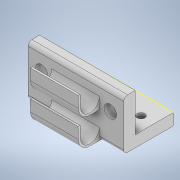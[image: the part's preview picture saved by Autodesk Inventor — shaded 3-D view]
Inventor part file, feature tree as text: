
AUTODESK INVENTOR PART (.ipt)
format: ipt  version: 2020 (Build 240168000, 168)  size: 246,784 bytes
history: native  units: in
note: dims shown in document units (in); Inventor stores cm internally (conversion verified against a paired STEP export)
features: sketch x7, extrude x4, plane x2, hole x2, direct_edit x1, fillet x1, mirror x1, move_body x1
ambient origin geometry x8: Origin, YZ Plane, XZ Plane, XY Plane, X Axis, Y Axis, Z Axis, Center Point
bodies: Solid1 (feature_tree)
feature tree (19):
  extrude  "Extrusion1"  Depth=1.0236in
  extrude  "Extrusion2"  Depth=0.7874in TaperAngle=0.0deg
  direct_edit  "Direct Edit1"
  extrude  "Extrusion7"  Depth=0.9843in
  plane  "Work Plane1"
  sketch  "Sketch8"  dims[d30=0.4724in d31=0.0in d45=0.3937in d58=0.0787in]
  extrude  "Extrusion15"  Depth=0.3937in
  fillet  "Fillet3"  Radius=0.0787in
  hole  "Hole1"  [1 undecoded]
  hole  "Hole2"  [1 undecoded]
  sketch  "Sketch13"  dims[d80=0.3937in d81=0.1969in d82=0.2362in d83=0.4724in d85=0.6322in d86=0.6322in d87=0.6322in d90=0.4724in d91=0.6322in d92=0.4724in d93=0.0in d94=0.0in d95=0.2362in d96=0.2362in d97=0.2756in d98=0.3937in d99=0.1575in d100=0.2362in d101=0.2559in d102=0.1772in d103=90.0deg d104=0.315in d105=0.8108in d106=0.2362in d107=0.3937in d108=0.2756in d109=0.1575in d110=0.2362in d111=0.2559in d112=0.1772in d113=90.0deg d114=0.315in d115=0.8108in d116=90.0deg d48=0.0197in d49=0.0344in d50=0.0197in d51=0.0344in d67=0.0197in d68=0.0344in d69=0.0197in d70=0.0344in d88=0.0197in d89=0.0344in]
  plane  "Work Plane3"
  mirror  "Mirror1"
  sketch  "Sketch1"  dims[d0=0.9843in d1=1.0236in]
  sketch  "Sketch2"  dims[d2=0.2362in d3=0.0in d5=0.7874in d6=0.0in]
  sketch  "Sketch7"  dims[d16=0.0in d17=0.0in d18=0.9843in d29=0.9843in]
  sketch  "Sketch11"  dims[d76=0.3937in d77=0.2362in]
  sketch  "Sketch12"  dims[d78=0.1969in d79=0.4724in]
  move_body  "Move1"
note: 2 required parameter values undecoded (feature->parameter linkage not recoverable at this tier; creation-order binding heuristic only, values carry confidence <= 0.55)
